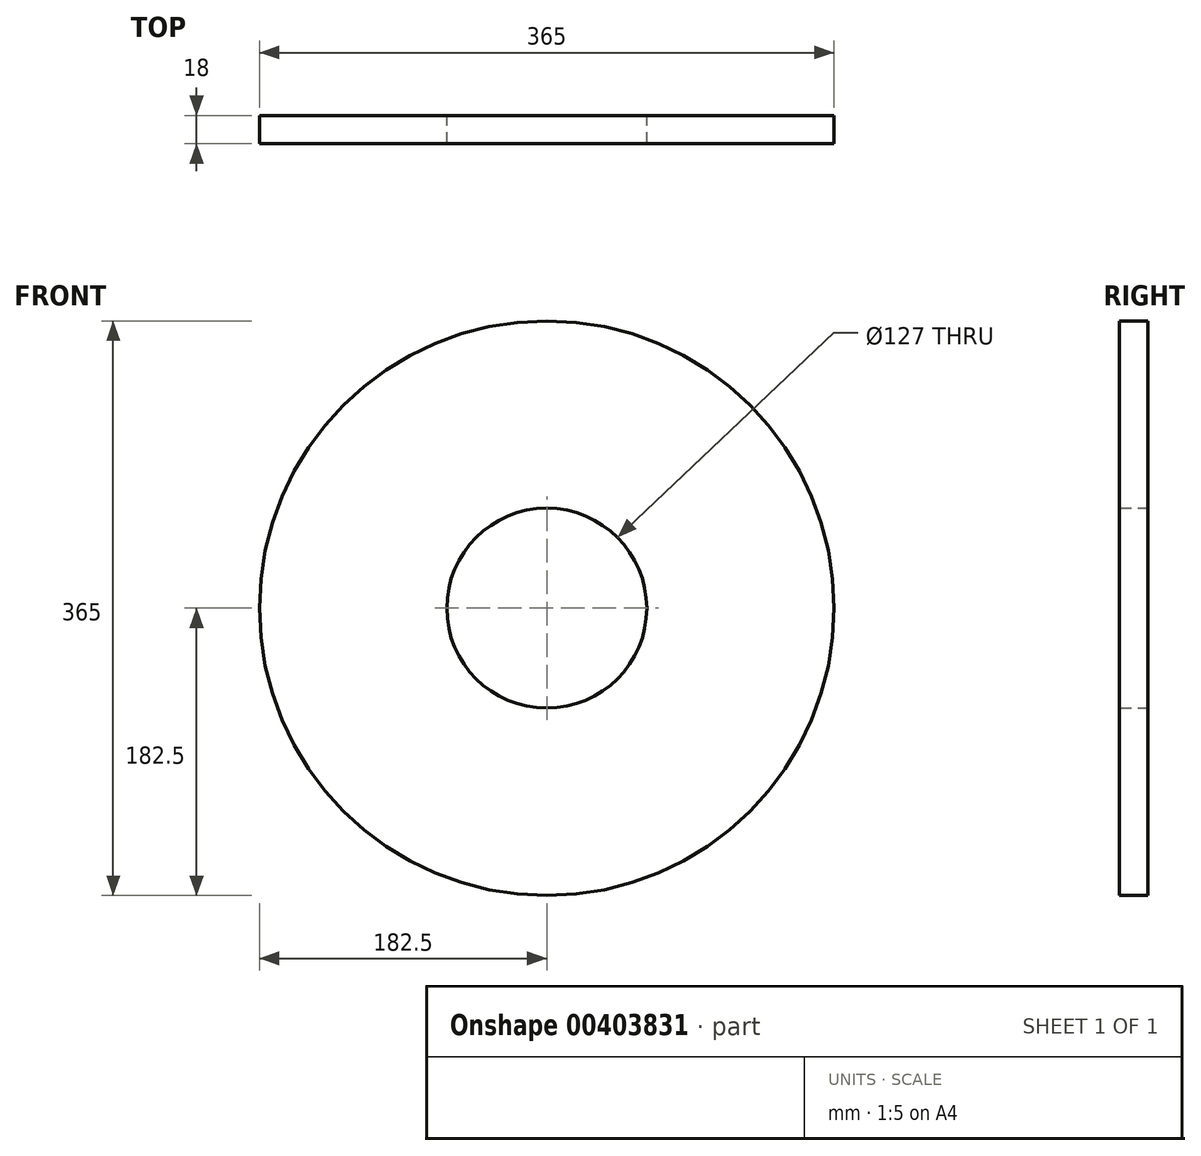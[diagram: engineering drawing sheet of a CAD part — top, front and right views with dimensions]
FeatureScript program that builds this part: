
annotation { "Feature Type Name" : "Feature", "Feature Type Description" : "" }
export const myFeature = defineFeature(function(context is Context, id is Id, definition is map)
    precondition{}
    {
        {
            var Q0;
            Q0=qCreatedBy(makeId("Front.planeOp"),FACE);
            var sketch = newSketch(context, id + "F0", { "sketchPlane" : qUnion([Q0])});
            skCircle(sketch, "E0", {"center": v(0, 0) * mm, "radius": 63.5 * mm});
            skCircle(sketch, "E1", {"center": v(0, 0) * mm, "radius": 182.5 * mm});
            skSolve(sketch);
        }
        {
            var Q0;
            Q0=makeQuery(id+"F0.imprint","IMPRINT",FACE,{"disambiguationData":[TD([[makeQuery(id+"F0.imprint","IMPRINT",EDGE,{"derivedFrom":sQuery(id+"F0.wireOp",EDGE,"E0")}),-1.0]])]});
            extrude(context, id + "F1", {"entities" : qUnion([Q0]), "depth" : 18 * mm});
        }
    });
